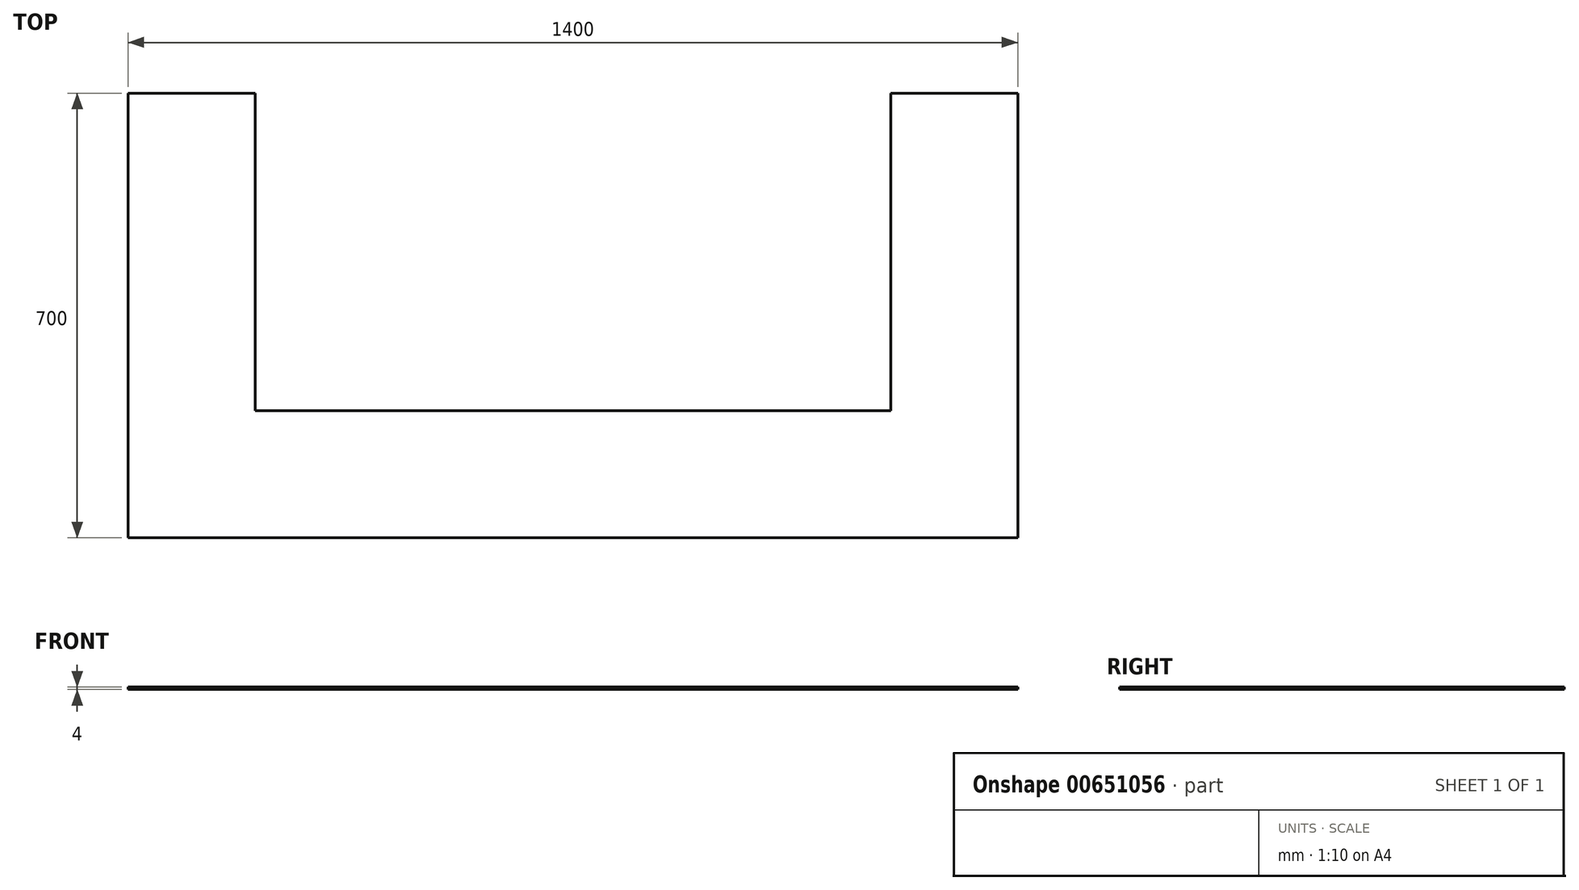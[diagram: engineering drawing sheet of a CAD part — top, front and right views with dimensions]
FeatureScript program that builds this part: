
annotation { "Feature Type Name" : "Feature", "Feature Type Description" : "" }
export const myFeature = defineFeature(function(context is Context, id is Id, definition is map)
    precondition{}
    {
        {
            var Q0;
            Q0=qCreatedBy(makeId("Top.planeOp"),FACE);
            var sketch = newSketch(context, id + "F0", { "sketchPlane" : qUnion([Q0])});
            skLineSegment(sketch, "E0.bottom", {"start": v(0, 0) * mm, "end": v(-1000, 0) * mm});
            skLineSegment(sketch, "E0.left", {"start": v(0, 0) * mm, "end": v(0, 500) * mm});
            skLineSegment(sketch, "E0.right", {"start": v(-1000, 0) * mm, "end": v(-1000, 500) * mm});
            skLineSegment(sketch, "E1.bottom", {"start": v(-1200, 500) * mm, "end": v(-1000, 500) * mm});
            skLineSegment(sketch, "E1.top", {"start": v(-1200, -200) * mm, "end": v(200, -200) * mm});
            skLineSegment(sketch, "E1.left", {"start": v(-1200, 500) * mm, "end": v(-1200, -200) * mm});
            skLineSegment(sketch, "E1.right", {"start": v(200, 500) * mm, "end": v(200, -200) * mm});
            skLineSegment(sketch, "E2.trimOffspring", {"start": v(0, 500) * mm, "end": v(200, 500) * mm});
            skSolve(sketch);
        }
        {
            var Q0;
            Q0=qSketchRegion(id+"F0",true);
            extrude(context, id + "F1", {"entities" : qUnion([Q0]), "depth" : 4 * mm, "offsetDistance" : 25 * mm});
        }
    });
